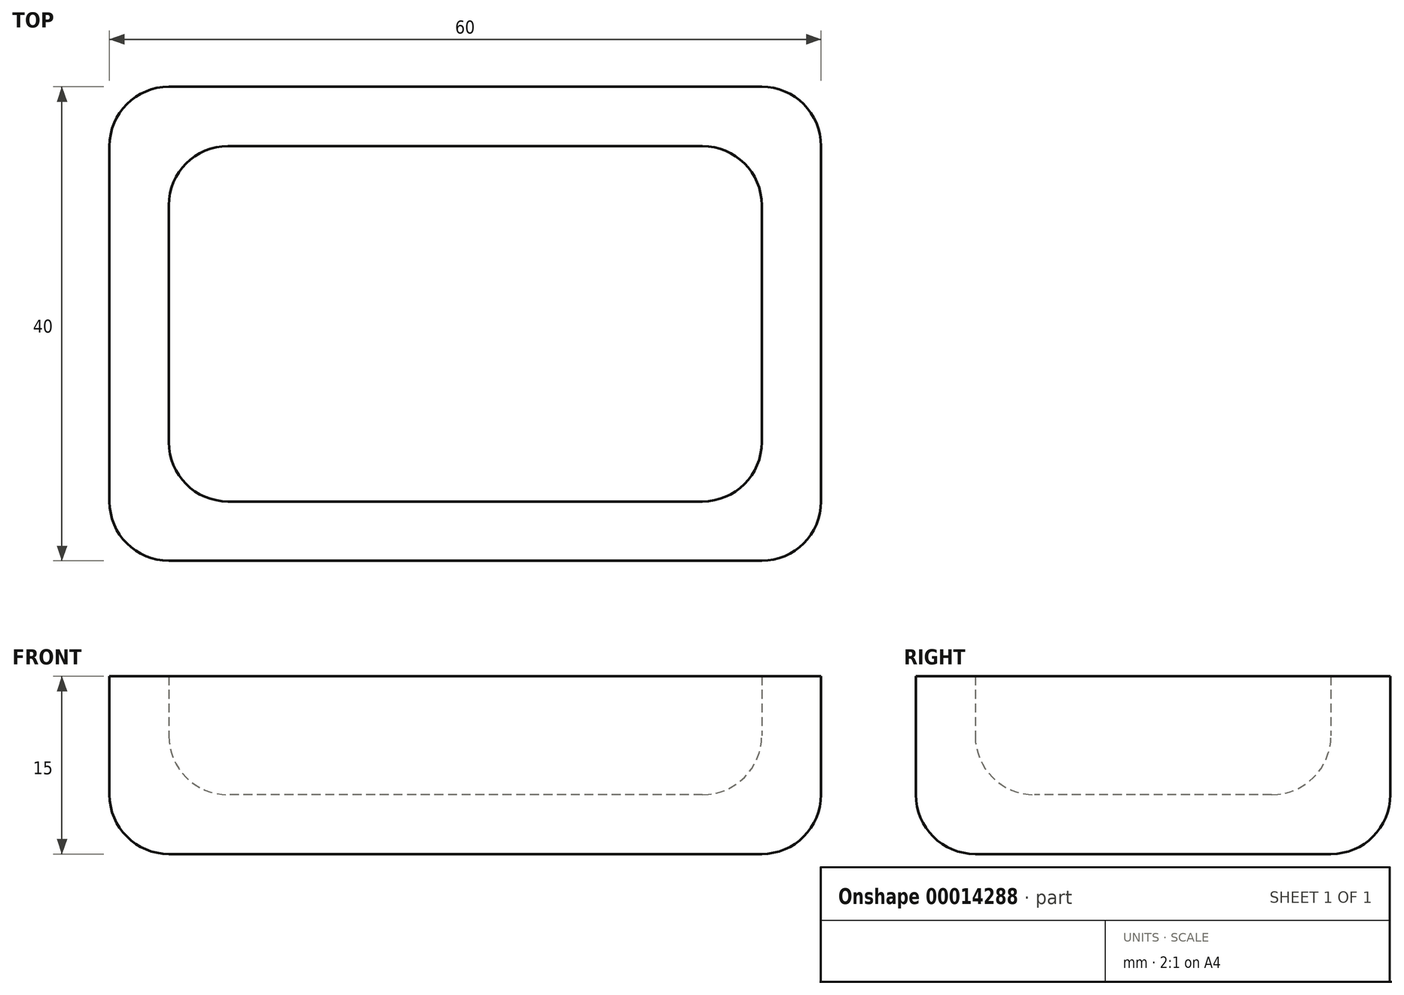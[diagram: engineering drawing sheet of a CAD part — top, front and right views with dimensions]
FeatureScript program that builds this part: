
annotation { "Feature Type Name" : "Feature", "Feature Type Description" : "" }
export const myFeature = defineFeature(function(context is Context, id is Id, definition is map)
    precondition{}
    {
        {
            var Q0;
            Q0=qCreatedBy(makeId("Top.planeOp"),FACE);
            var sketch = newSketch(context, id + "F0", { "sketchPlane" : qUnion([Q0])});
            skLineSegment(sketch, "E0.rect.bottom", {"start": v(30, 20) * mm, "end": v(-30, 20) * mm});
            skLineSegment(sketch, "E0.rect.top", {"start": v(30, -20) * mm, "end": v(-30, -20) * mm});
            skLineSegment(sketch, "E0.rect.left", {"start": v(30, 20) * mm, "end": v(30, -20) * mm});
            skLineSegment(sketch, "E0.rect.right", {"start": v(-30, 20) * mm, "end": v(-30, -20) * mm});
            skPoint(sketch, "E0.rect.middle", {"position": v(0, 0) * mm});
            skSolve(sketch);
        }
        {
            var Q0;
            Q0=makeQuery(id+"F0.imprint","IMPRINT",FACE,{"disambiguationData":[TD([[makeQuery(id+"F0.imprint","IMPRINT",EDGE,{"derivedFrom":sQuery(id+"F0.wireOp",EDGE,"E0.rect.bottom")}),1.0]])]});
            extrude(context, id + "F1", {"entities" : qUnion([Q0]), "depth" : 15 * mm});
        }
        {
            var Q0;
            Q0=makeQuery(id+"F1.opExtrude","CAP_FACE",FACE,{"disambiguationData":[OSD([sQuery(id+"F0.wireOp",EDGE,"E0.rect.bottom"),sQuery(id+"F0.wireOp",EDGE,"E0.rect.top"),sQuery(id+"F0.wireOp",EDGE,"E0.rect.left"),sQuery(id+"F0.wireOp",EDGE,"E0.rect.right")])],"isStart":false});
            shell(context, id + "F2", {"entities" : qUnion([Q0]), "thickness" : 5 * mm});
        }
        {
            var Q0;
            Q0=makeQuery(id+"F2.opShell","OFFSET_EDGE",EDGE,{"disambiguationData":[OSD([sQuery(id+"F0.wireOp",EDGE,"E0.rect.bottom"),sQuery(id+"F0.wireOp",EDGE,"E0.rect.left")])]});
            var Q1;
            Q1=makeQuery(id+"F2.opShell","OFFSET_EDGE",EDGE,{"disambiguationData":[OSD([sQuery(id+"F0.wireOp",EDGE,"E0.rect.bottom"),sQuery(id+"F0.wireOp",EDGE,"E0.rect.right")])]});
            var Q2;
            Q2=makeQuery(id+"F2.opShell","OFFSET_EDGE",EDGE,{"disambiguationData":[OSD([sQuery(id+"F0.wireOp",EDGE,"E0.rect.top"),sQuery(id+"F0.wireOp",EDGE,"E0.rect.left")])]});
            var Q3;
            Q3=makeQuery(id+"F2.opShell","OFFSET_EDGE",EDGE,{"disambiguationData":[OSD([sQuery(id+"F0.wireOp",EDGE,"E0.rect.top"),sQuery(id+"F0.wireOp",EDGE,"E0.rect.right")])]});
            var Q4;
            Q4=makeQuery(id+"F2.opShell","OFFSET_FACE",FACE,{"disambiguationData":[OSD([sQuery(id+"F0.wireOp",EDGE,"E0.rect.bottom"),sQuery(id+"F0.wireOp",EDGE,"E0.rect.top"),sQuery(id+"F0.wireOp",EDGE,"E0.rect.left"),sQuery(id+"F0.wireOp",EDGE,"E0.rect.right")])]});
            var Q5;
            Q5=makeQuery(id+"F1.opExtrude","SWEPT_EDGE",EDGE,{"disambiguationData":[OSD([sQuery(id+"F0.wireOp",EDGE,"E0.rect.top"),sQuery(id+"F0.wireOp",EDGE,"E0.rect.right")])]});
            var Q6;
            Q6=makeQuery(id+"F1.opExtrude","SWEPT_EDGE",EDGE,{"disambiguationData":[OSD([sQuery(id+"F0.wireOp",EDGE,"E0.rect.bottom"),sQuery(id+"F0.wireOp",EDGE,"E0.rect.right")])]});
            var Q7;
            Q7=makeQuery(id+"F1.opExtrude","SWEPT_EDGE",EDGE,{"disambiguationData":[OSD([sQuery(id+"F0.wireOp",EDGE,"E0.rect.top"),sQuery(id+"F0.wireOp",EDGE,"E0.rect.left")])]});
            var Q8;
            Q8=makeQuery(id+"F1.opExtrude","SWEPT_EDGE",EDGE,{"disambiguationData":[OSD([sQuery(id+"F0.wireOp",EDGE,"E0.rect.bottom"),sQuery(id+"F0.wireOp",EDGE,"E0.rect.left")])]});
            var Q9;
            Q9=makeQuery(id+"F1.opExtrude","CAP_FACE",FACE,{"disambiguationData":[OSD([sQuery(id+"F0.wireOp",EDGE,"E0.rect.bottom"),sQuery(id+"F0.wireOp",EDGE,"E0.rect.top"),sQuery(id+"F0.wireOp",EDGE,"E0.rect.left"),sQuery(id+"F0.wireOp",EDGE,"E0.rect.right")])],"isStart":true});
            fillet(context, id + "F3", {"entities" : qUnion([Q0, Q1, Q2, Q3, Q4, Q5, Q6, Q7, Q8, Q9]), "radius" : 5 * mm, "tangentPropagation" : true, "allowEdgeOverflow" : false});
        }
    });
